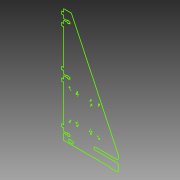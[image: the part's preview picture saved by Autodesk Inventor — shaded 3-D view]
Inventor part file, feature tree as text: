
AUTODESK INVENTOR PART (.ipt)
format: ipt  version: 2015 (Build 190159000, 159)  size: 230,400 bytes
history: native  units: mm
features: sketch x1
ambient origin geometry x8: Origin, YZ Plane, XZ Plane, XY Plane, X Axis, Y Axis, Z Axis, Center Point
feature tree (1):
  sketch  "Sketch1"
